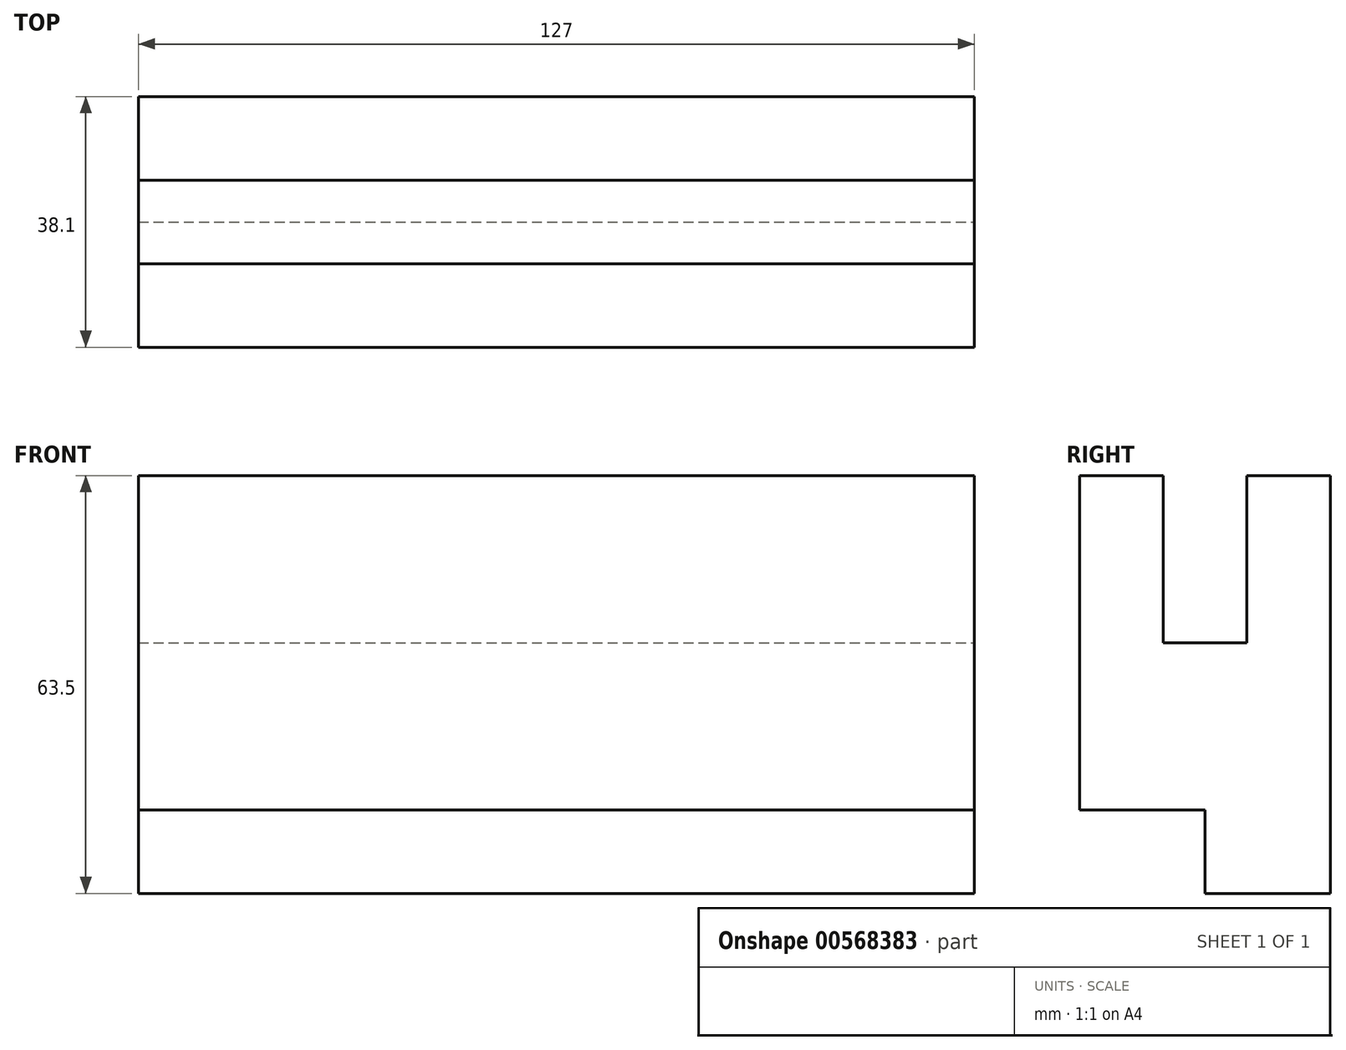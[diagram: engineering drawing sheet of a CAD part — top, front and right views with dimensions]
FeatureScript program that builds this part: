
annotation { "Feature Type Name" : "Feature", "Feature Type Description" : "" }
export const myFeature = defineFeature(function(context is Context, id is Id, definition is map)
    precondition{}
    {
        {
            var Q0;
            Q0=qCreatedBy(makeId("Right.planeOp"),FACE);
            var sketch = newSketch(context, id + "F0", { "sketchPlane" : qUnion([Q0])});
            skLineSegment(sketch, "E0.bottom", {"start": v(0, 0) * mm, "end": v(-38.1, 0) * mm});
            skLineSegment(sketch, "E0.top", {"start": v(0, 63.5) * mm, "end": v(-38.1, 63.5) * mm});
            skLineSegment(sketch, "E0.left", {"start": v(0, 0) * mm, "end": v(0, 63.5) * mm});
            skLineSegment(sketch, "E0.right", {"start": v(-38.1, 0) * mm, "end": v(-38.1, 63.5) * mm});
            skSolve(sketch);
        }
        {
            var Q0;
            Q0 = qSketchRegion(id + "F0", true);
            extrude(context, id + "F1", {"entities" : qUnion([Q0]), "depth" : 127 * mm, "offsetDistance" : 25.4 * mm});
        }
        {
            var Q0;
            Q0=makeQuery(id+"F1.opExtrude","CAP_FACE",FACE,{"disambiguationData":[OSD([sQuery(id+"F0.wireOp",EDGE,"E0.bottom"),sQuery(id+"F0.wireOp",EDGE,"E0.top"),sQuery(id+"F0.wireOp",EDGE,"E0.left"),sQuery(id+"F0.wireOp",EDGE,"E0.right")])],"isStart":false});
            var sketch = newSketch(context, id + "F2", { "sketchPlane" : qUnion([Q0])});
            skLineSegment(sketch, "E1.bottom", {"start": v(-38.1, 0) * mm, "end": v(-19.05, 0) * mm});
            skLineSegment(sketch, "E1.top", {"start": v(-38.1, 12.7) * mm, "end": v(-19.05, 12.7) * mm});
            skLineSegment(sketch, "E1.left", {"start": v(-38.1, 0) * mm, "end": v(-38.1, 12.7) * mm});
            skLineSegment(sketch, "E1.right", {"start": v(-19.05, 0) * mm, "end": v(-19.05, 12.7) * mm});
            skSolve(sketch);
        }
        {
            var Q0;
            Q0 = qSketchRegion(id + "F2", true);
            extrude(context, id + "F3", {"entities" : qUnion([Q0]), "operationType" : NewBodyOperationType.REMOVE, "endBound" : BoundingType.THROUGH_ALL, "oppositeDirection" : true, "depth" : 25.4 * mm, "offsetDistance" : 25.4 * mm});
        }
        {
            var Q0;
            Q0=makeQuery(id+"F1.opExtrude","CAP_FACE",FACE,{"disambiguationData":[OSD([sQuery(id+"F0.wireOp",EDGE,"E0.bottom"),sQuery(id+"F0.wireOp",EDGE,"E0.top"),sQuery(id+"F0.wireOp",EDGE,"E0.left"),sQuery(id+"F0.wireOp",EDGE,"E0.right")])],"isStart":false});
            var sketch = newSketch(context, id + "F4", { "sketchPlane" : qUnion([Q0])});
            skLineSegment(sketch, "E2.bottom", {"start": v(-12.7, 63.5) * mm, "end": v(-25.4, 63.5) * mm});
            skLineSegment(sketch, "E2.top", {"start": v(-12.7, 38.1) * mm, "end": v(-25.4, 38.1) * mm});
            skLineSegment(sketch, "E2.left", {"start": v(-12.7, 63.5) * mm, "end": v(-12.7, 38.1) * mm});
            skLineSegment(sketch, "E2.right", {"start": v(-25.4, 63.5) * mm, "end": v(-25.4, 38.1) * mm});
            skSolve(sketch);
        }
        {
            var Q0;
            Q0 = qSketchRegion(id + "F4", true);
            extrude(context, id + "F5", {"entities" : qUnion([Q0]), "operationType" : NewBodyOperationType.REMOVE, "endBound" : BoundingType.THROUGH_ALL, "oppositeDirection" : true, "depth" : 25.4 * mm, "offsetDistance" : 25.4 * mm});
        }
    });
